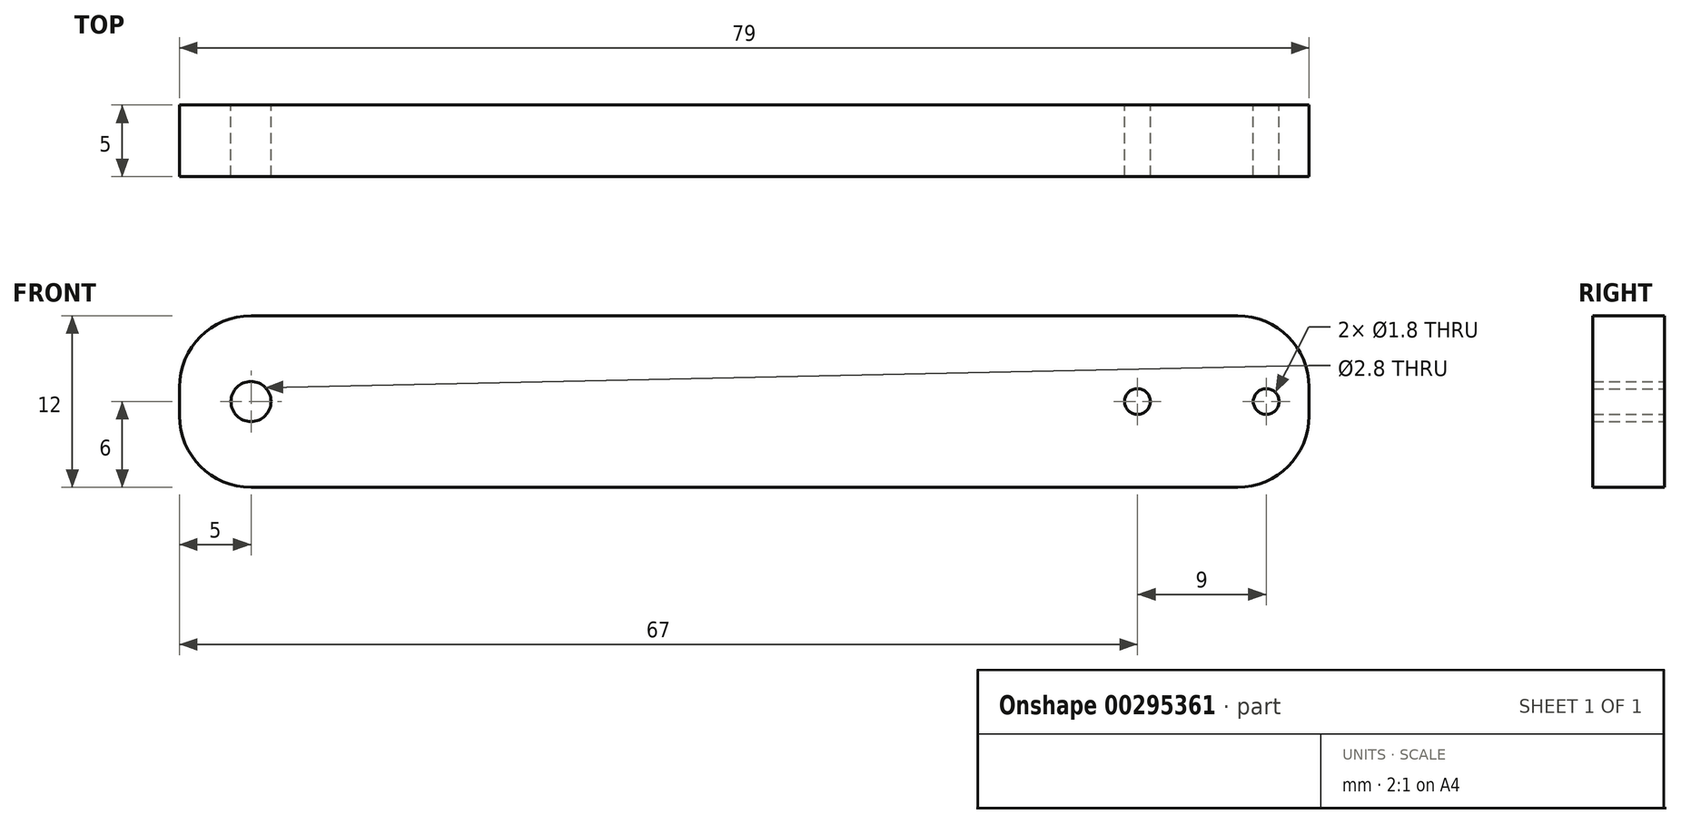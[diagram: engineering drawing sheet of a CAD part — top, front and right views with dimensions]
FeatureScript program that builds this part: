
annotation { "Feature Type Name" : "Feature", "Feature Type Description" : "" }
export const myFeature = defineFeature(function(context is Context, id is Id, definition is map)
    precondition{}
    {
        {
            var Q0;
            Q0=qCreatedBy(makeId("Front.planeOp"),FACE);
            var sketch = newSketch(context, id + "F0", { "sketchPlane" : qUnion([Q0])});
            skCircle(sketch, "E0", {"center": v(-80, 0) * mm, "radius": 1.4 * mm});
            skLineSegment(sketch, "E1.bottom", {"start": v(-11, -6) * mm, "end": v(-80, -6) * mm});
            skLineSegment(sketch, "E1.top", {"start": v(-11, 6) * mm, "end": v(-80, 6) * mm});
            skLineSegment(sketch, "E1.right", {"start": v(-85, -1) * mm, "end": v(-85, 1) * mm});
            skCircle(sketch, "E2", {"center": v(-9, 0) * mm, "radius": 0.9 * mm});
            skCircle(sketch, "E3", {"center": v(-18, 0) * mm, "radius": 0.9 * mm});
            skPoint(sketch, "E4", {"position": v(-2, 0) * mm});
            skPoint(sketch, "E5", {"position": v(8, 0) * mm});
            skLineSegment(sketch, "E6", {"start": v(-6, -1) * mm, "end": v(-6, 1) * mm});
            skPoint(sketch, "E7.visualSharp", {"position": v(-85, 6) * mm});
            skArc(sketch, "E7.filletArc", {"start": v(-80, 6) * mm, "mid": v(-83.54, 4.54) * mm, "end": v(-85, 1) * mm});
            skPoint(sketch, "E8.visualSharp", {"position": v(-85, -6) * mm});
            skArc(sketch, "E8.filletArc", {"start": v(-85, -1) * mm, "mid": v(-83.54, -4.54) * mm, "end": v(-80, -6) * mm});
            skPoint(sketch, "E9.visualSharp", {"position": v(-6, -6) * mm});
            skArc(sketch, "E9.filletArc", {"start": v(-11, -6) * mm, "mid": v(-7.46, -4.54) * mm, "end": v(-6, -1) * mm});
            skPoint(sketch, "E10.visualSharp", {"position": v(-6, 6) * mm});
            skArc(sketch, "E10.filletArc", {"start": v(-6, 1) * mm, "mid": v(-7.46, 4.54) * mm, "end": v(-11, 6) * mm});
            skSolve(sketch);
        }
        {
            var Q0;
            Q0=makeQuery(id+"F0.imprint","IMPRINT",FACE,{"disambiguationData":[TD([[makeQuery(id+"F0.imprint","IMPRINT",EDGE,{"derivedFrom":sQuery(id+"F0.wireOp",EDGE,"E0")}),-1.0]])]});
            extrude(context, id + "F1", {"entities" : qUnion([Q0]), "depth" : 5 * mm});
        }
    });
